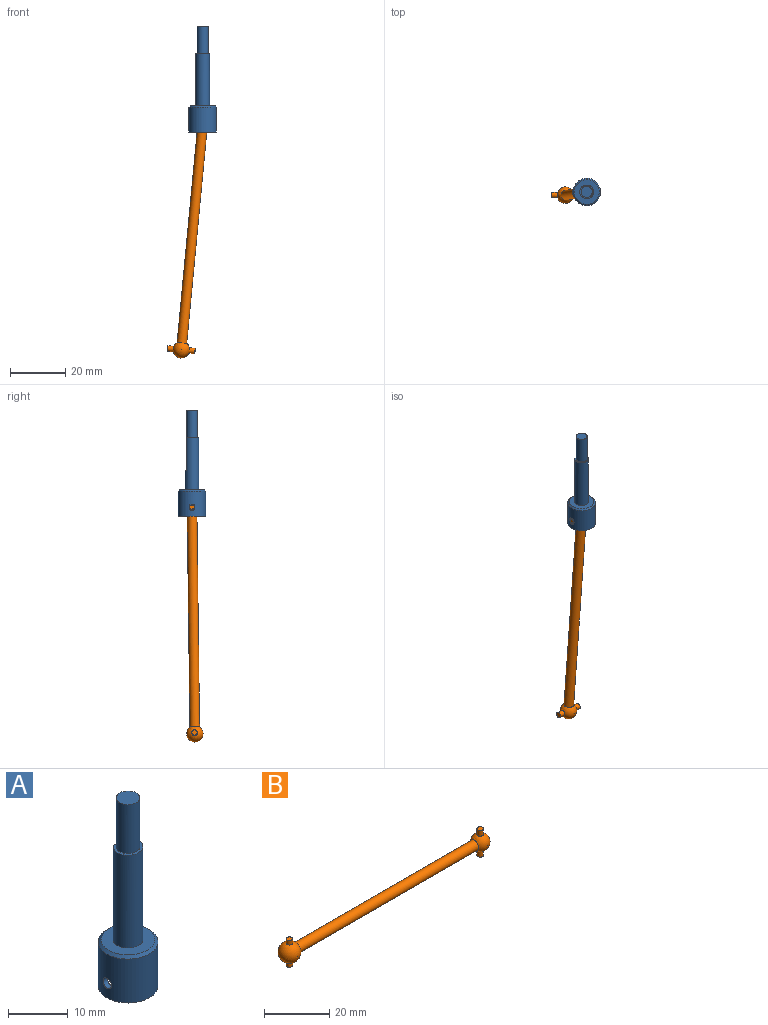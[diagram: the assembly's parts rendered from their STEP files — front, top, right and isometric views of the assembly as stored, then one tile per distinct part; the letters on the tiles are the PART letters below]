
ASSEMBLY  parts=2 mates=1
PART A: 14 faces, bbox 10x10x38.5 mm
  f0: cylinder r=2.5mm len=19mm, axis (0,0,-1), area 259.8mm2, adj f1,f5,f12,f13
  f1: plane 5x4.5mm, normal (0,0,1), area 6mm2, adj f0,f2,f13
  f2: cylinder r=2mm len=10mm, axis (0,0,-1), area 125.7mm2, adj f1,f3
  f3: plane 4x4mm, normal (0,0,1), area 12.6mm2, adj f2
  f4: cylinder r=5mm len=10mm, axis (0,0,1), area 276.4mm2, adj f7,f9,f10,f11
  f5: plane 9x9mm, normal (0,0,1), area 44mm2, adj f0,f11
  f6: cylinder r=4mm len=8.5mm, axis (0,0,1), area 207.3mm2, adj f7,f8,f9,f10
  f7: plane 10x10mm, normal (0,0,-1), area 28.3mm2, adj f4,f6
  f8: plane 8x8mm, normal (0,0,-1), area 50.3mm2, adj f6
  f9: cylinder r=1mm len=2mm, axis (1,0,0), area 6.4mm2, adj f4,f6
  f10: cylinder r=1mm len=2mm, axis (1,0,0), area 6.4mm2, adj f4,f6
  f11: cone r=4.5mm half-angle=45deg, axis (0,0,-1), area 21.1mm2, adj f4,f5
  f12: plane 3x0.5mm, normal (0,0,1), area 1mm2, adj f0,f13
  f13: plane 12x3mm, normal (0,1,0), area 36mm2, adj f0,f1,f12
PART B: 11 faces, bbox 89x7x10 mm
  f0: sphere r=3mm, area 96mm2, adj f2,f8,f9
  f1: sphere r=3.5mm, area 137.2mm2, adj f2,f4,f5
  f2: cylinder r=1.75mm len=77.03mm, axis (-1,0,0), area 847mm2, adj f0,f1
  f3: plane 2x2mm, normal (0,0,1), area 3.1mm2, adj f4
  f4: cylinder r=1mm len=2mm, axis (0,0,-1), area 10.3mm2, adj f1,f3
  f5: cylinder r=1mm len=2mm, axis (0,0,-1), area 10.3mm2, adj f1,f6
  f6: plane 2x2mm, normal (0,0,-1), area 3.1mm2, adj f5
  f7: plane 2x2mm, normal (0,0,1), area 3.1mm2, adj f8
  f8: cylinder r=1mm len=2.17mm, axis (0,0,-1), area 13.6mm2, adj f0,f7
  f9: cylinder r=1mm len=2.17mm, axis (0,0,-1), area 13.6mm2, adj f0,f10
  f10: plane 2x2mm, normal (0,0,-1), area 3.1mm2, adj f9
PLACE A t=(6.8,-2.87,-19.94)mm fixed
PLACE B rot(axis=(0,1,-0.01),95.4deg) t=(6.81,-2.87,-26.41)mm
MATE ball A.f6 <-> B.f2  axis (0,0,1) through (6.8,-2.87,-26.44)mm
